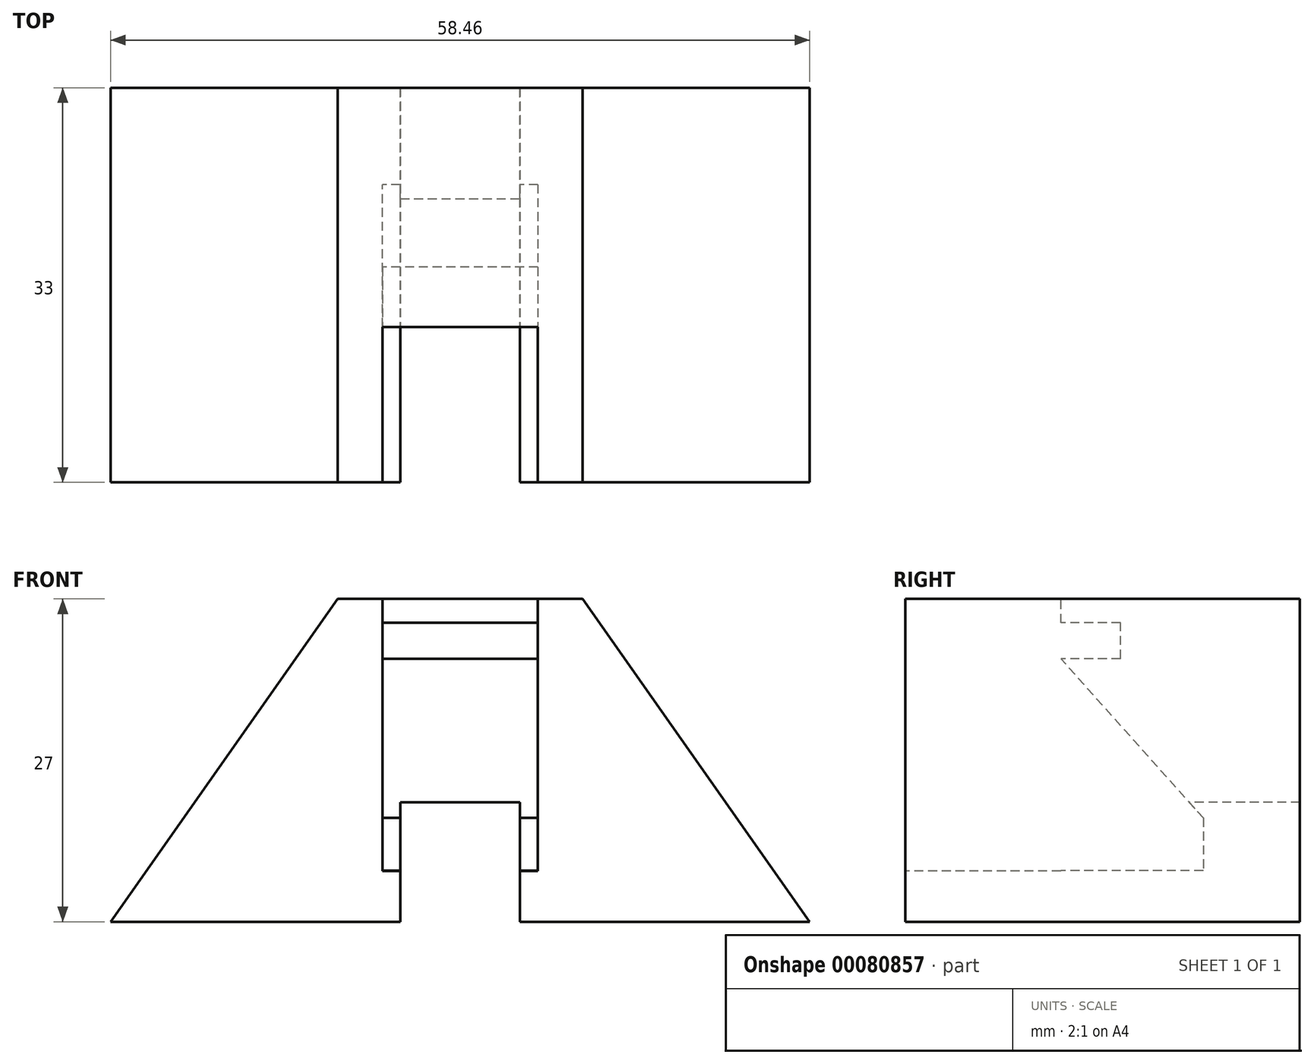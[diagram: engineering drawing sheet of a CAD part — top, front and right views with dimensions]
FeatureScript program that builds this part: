
annotation { "Feature Type Name" : "Feature", "Feature Type Description" : "" }
export const myFeature = defineFeature(function(context is Context, id is Id, definition is map)
    precondition{}
    {
        {
            var Q0;
            Q0=qCreatedBy(makeId("Top.planeOp"),FACE);
            var sketch = newSketch(context, id + "F0", { "sketchPlane" : qUnion([Q0])});
            skLineSegment(sketch, "E0.bottom", {"start": v(29.23, 16.5) * mm, "end": v(-29.22, 16.5) * mm});
            skLineSegment(sketch, "E0.top", {"start": v(29.23, -16.5) * mm, "end": v(-29.23, -16.5) * mm});
            skLineSegment(sketch, "E0.left", {"start": v(29.23, 16.5) * mm, "end": v(29.23, -16.5) * mm});
            skLineSegment(sketch, "E0.right", {"start": v(-29.22, 16.5) * mm, "end": v(-29.23, -16.5) * mm});
            skPoint(sketch, "E0.middle", {"position": v(0, 0) * mm});
            skSolve(sketch);
        }
        {
            var Q0;
            Q0=qSketchRegion(id+"F0",true);
            extrude(context, id + "F1", {"entities" : qUnion([Q0]), "depth" : 27 * mm});
        }
        {
            var Q0;
            Q0=makeQuery(id+"F1.opExtrude","SWEPT_FACE",FACE,{"disambiguationData":[OSD([sQuery(id+"F0.wireOp",EDGE,"E0.top")])]});
            var sketch = newSketch(context, id + "F2", { "sketchPlane" : qUnion([Q0])});
            skLineSegment(sketch, "E1", {"start": v(-29.23, 0) * mm, "end": v(-10.25, 27) * mm});
            skLineSegment(sketch, "E2", {"start": v(-10.25, 27) * mm, "end": v(-10.25, 0) * mm});
            skLineSegment(sketch, "E3", {"start": v(-10.25, 0) * mm, "end": v(-29.23, 0) * mm});
            skLineSegment(sketch, "E4", {"start": v(29.23, 0) * mm, "end": v(10.25, 27) * mm});
            skLineSegment(sketch, "E5", {"start": v(10.25, 27) * mm, "end": v(10.25, 0) * mm});
            skLineSegment(sketch, "E6", {"start": v(10.25, 0) * mm, "end": v(29.23, 0) * mm});
            skSolve(sketch);
        }
        {
            var Q0;
            {var subQ0=sQuery(id+"F2.wireOp",EDGE,"E1");Q0=makeQuery(id+"F2.imprint","IMPRINT",FACE,{"disambiguationData":[TD([[makeQuery(id+"F2.imprint","IMPRINT",EDGE,{"derivedFrom":subQ0}),1.0]])]});}
            var Q1;
            {var subQ0=sQuery(id+"F2.wireOp",EDGE,"E4");Q1=makeQuery(id+"F2.imprint","IMPRINT",FACE,{"disambiguationData":[TD([[makeQuery(id+"F2.imprint","IMPRINT",EDGE,{"derivedFrom":subQ0}),-1.0]])]});}
            extrude(context, id + "F3", {"entities" : qUnion([Q0, Q1]), "operationType" : NewBodyOperationType.REMOVE, "oppositeDirection" : true, "depth" : 33 * mm});
        }
        {
            var Q0;
            Q0=makeQuery(id+"F1.opExtrude","CAP_FACE",FACE,{"disambiguationData":[OSD([sQuery(id+"F0.wireOp",EDGE,"E0.bottom"),sQuery(id+"F0.wireOp",EDGE,"E0.top"),sQuery(id+"F0.wireOp",EDGE,"E0.left"),sQuery(id+"F0.wireOp",EDGE,"E0.right")])],"isStart":false});
            var sketch = newSketch(context, id + "F4", { "sketchPlane" : qUnion([Q0])});
            skLineSegment(sketch, "E7.bottom", {"start": v(5, -16.5) * mm, "end": v(-5, -16.5) * mm});
            skLineSegment(sketch, "E7.top", {"start": v(5, -3.5) * mm, "end": v(-5, -3.5) * mm});
            skLineSegment(sketch, "E7.left", {"start": v(5, -16.5) * mm, "end": v(5, -3.5) * mm});
            skLineSegment(sketch, "E7.right", {"start": v(-5, -16.5) * mm, "end": v(-5, -3.5) * mm});
            skPoint(sketch, "E7.middle", {"position": v(0, -10) * mm});
            skSolve(sketch);
        }
        {
            var Q0;
            Q0=qSketchRegion(id+"F4",true);
            extrude(context, id + "F5", {"entities" : qUnion([Q0]), "operationType" : NewBodyOperationType.REMOVE, "oppositeDirection" : true, "depth" : 27 * mm});
        }
        {
            var Q0;
            Q0=makeQuery(id+"F1.opExtrude","CAP_FACE",FACE,{"disambiguationData":[OSD([sQuery(id+"F0.wireOp",EDGE,"E0.bottom"),sQuery(id+"F0.wireOp",EDGE,"E0.top"),sQuery(id+"F0.wireOp",EDGE,"E0.left"),sQuery(id+"F0.wireOp",EDGE,"E0.right")])],"isStart":false});
            var sketch = newSketch(context, id + "F6", { "sketchPlane" : qUnion([Q0])});
            skLineSegment(sketch, "E8.bottom", {"start": v(6.5, -16.5) * mm, "end": v(-6.5, -16.5) * mm});
            skLineSegment(sketch, "E8.top", {"start": v(6.5, -3.5) * mm, "end": v(-6.5, -3.5) * mm});
            skLineSegment(sketch, "E8.left", {"start": v(6.5, -16.5) * mm, "end": v(6.5, -3.5) * mm});
            skLineSegment(sketch, "E8.right", {"start": v(-6.5, -16.5) * mm, "end": v(-6.5, -3.5) * mm});
            skPoint(sketch, "E8.middle", {"position": v(0, -10) * mm});
            skPoint(sketch, "E8.middle.positionSnap0", {"position": v(5, -10) * mm});
            skPoint(sketch, "E8.middle.positionSnap1", {"position": v(0, -3.5) * mm});
            skPoint(sketch, "E8.centerSnap0", {"position": v(5, -10) * mm});
            skPoint(sketch, "E8.centerSnap1", {"position": v(0, -3.5) * mm});
            skSolve(sketch);
        }
        {
            var Q0;
            Q0=qSketchRegion(id+"F6",true);
            extrude(context, id + "F7", {"entities" : qUnion([Q0]), "operationType" : NewBodyOperationType.REMOVE, "oppositeDirection" : true, "depth" : 22.75 * mm});
        }
        {
            var Q0;
            Q0=makeQuery(id+"F7.boolean.opBoolean","MERGE",FACE,{"derivedFrom":[makeQuery(id+"F5.boolean.opBoolean","COPY",FACE,{"derivedFrom":makeQuery(id+"F5.opExtrude","SWEPT_FACE",FACE,{"disambiguationData":[OSD([sQuery(id+"F4.wireOp",EDGE,"E7.top")])]})}),makeQuery(id+"F7.opExtrude","SWEPT_FACE",FACE,{"disambiguationData":[OSD([sQuery(id+"F6.wireOp",EDGE,"E8.top")])]})]});
            var sketch = newSketch(context, id + "F8", { "sketchPlane" : qUnion([Q0])});
            skLineSegment(sketch, "E9.bottom", {"start": v(6.5, 22) * mm, "end": v(-6.5, 22) * mm});
            skLineSegment(sketch, "E9.top", {"start": v(6.5, 25) * mm, "end": v(-6.5, 25) * mm});
            skLineSegment(sketch, "E9.left", {"start": v(6.5, 22) * mm, "end": v(6.5, 25) * mm});
            skLineSegment(sketch, "E9.right", {"start": v(-6.5, 22) * mm, "end": v(-6.5, 25) * mm});
            skPoint(sketch, "E9.middle", {"position": v(0, 23.5) * mm});
            skSolve(sketch);
        }
        {
            var Q0;
            Q0=qSketchRegion(id+"F8",true);
            extrude(context, id + "F9", {"entities" : qUnion([Q0]), "operationType" : NewBodyOperationType.REMOVE, "oppositeDirection" : true, "depth" : 5 * mm});
        }
        {
            var Q0;
            {var subQ2=sQuery(id+"F6.wireOp",EDGE,"E8.top");Q0=makeQuery(id+"F9.boolean.opBoolean","SPLIT",FACE,{"disambiguationData":[TD([makeQuery(id+"F5.boolean.opBoolean","COPY",FACE,{"derivedFrom":makeQuery(id+"F5.opExtrude","SWEPT_FACE",FACE,{"disambiguationData":[OSD([sQuery(id+"F4.wireOp",EDGE,"E7.left")])]})})])],"derivedFrom":makeQuery(id+"F7.boolean.opBoolean","MERGE",FACE,{"derivedFrom":[makeQuery(id+"F5.boolean.opBoolean","COPY",FACE,{"derivedFrom":makeQuery(id+"F5.opExtrude","SWEPT_FACE",FACE,{"disambiguationData":[OSD([sQuery(id+"F4.wireOp",EDGE,"E7.top")])]})}),makeQuery(id+"F7.opExtrude","SWEPT_FACE",FACE,{"disambiguationData":[OSD([subQ2])]})]})});}
            var sketch = newSketch(context, id + "F10", { "sketchPlane" : qUnion([Q0])});
            skLineSegment(sketch, "E10.bottom", {"start": v(5, 0) * mm, "end": v(-5, 0) * mm});
            skLineSegment(sketch, "E10.top", {"start": v(5, 10) * mm, "end": v(-5, 10) * mm});
            skLineSegment(sketch, "E10.left", {"start": v(5, 0) * mm, "end": v(5, 10) * mm});
            skLineSegment(sketch, "E10.right", {"start": v(-5, 0) * mm, "end": v(-5, 10) * mm});
            skPoint(sketch, "E10.middle", {"position": v(0, 5) * mm});
            skSolve(sketch);
        }
        {
            var Q0;
            Q0=qSketchRegion(id+"F10",true);
            extrude(context, id + "F11", {"entities" : qUnion([Q0]), "operationType" : NewBodyOperationType.REMOVE, "oppositeDirection" : true, "depth" : 33 * mm});
        }
        {
            var Q0;
            Q0=qCreatedBy(makeId("Right.planeOp"),FACE);
            var sketch = newSketch(context, id + "F12", { "sketchPlane" : qUnion([Q0])});
            skLineSegment(sketch, "E11", {"start": v(-3.5, 4.26) * mm, "end": v(8.41, 4.26) * mm});
            skLineSegment(sketch, "E12", {"start": v(8.41, 4.26) * mm, "end": v(8.41, 8.68) * mm});
            skLineSegment(sketch, "E13", {"start": v(8.41, 8.68) * mm, "end": v(-3.5, 22) * mm});
            skLineSegment(sketch, "E14", {"start": v(-3.5, 22) * mm, "end": v(-3.5, 4.26) * mm});
            skLineSegment(sketch, "E15", {"start": v(-3.5, 22) * mm, "end": v(48.87, 22) * mm, "construction": true});
            skSolve(sketch);
        }
        {
            var Q0;
            Q0=qSketchRegion(id+"F12",true);
            extrude(context, id + "F13", {"entities" : qUnion([Q0]), "operationType" : NewBodyOperationType.REMOVE, "endBound" : BoundingType.SYMMETRIC, "depth" : 13 * mm});
        }
    });
